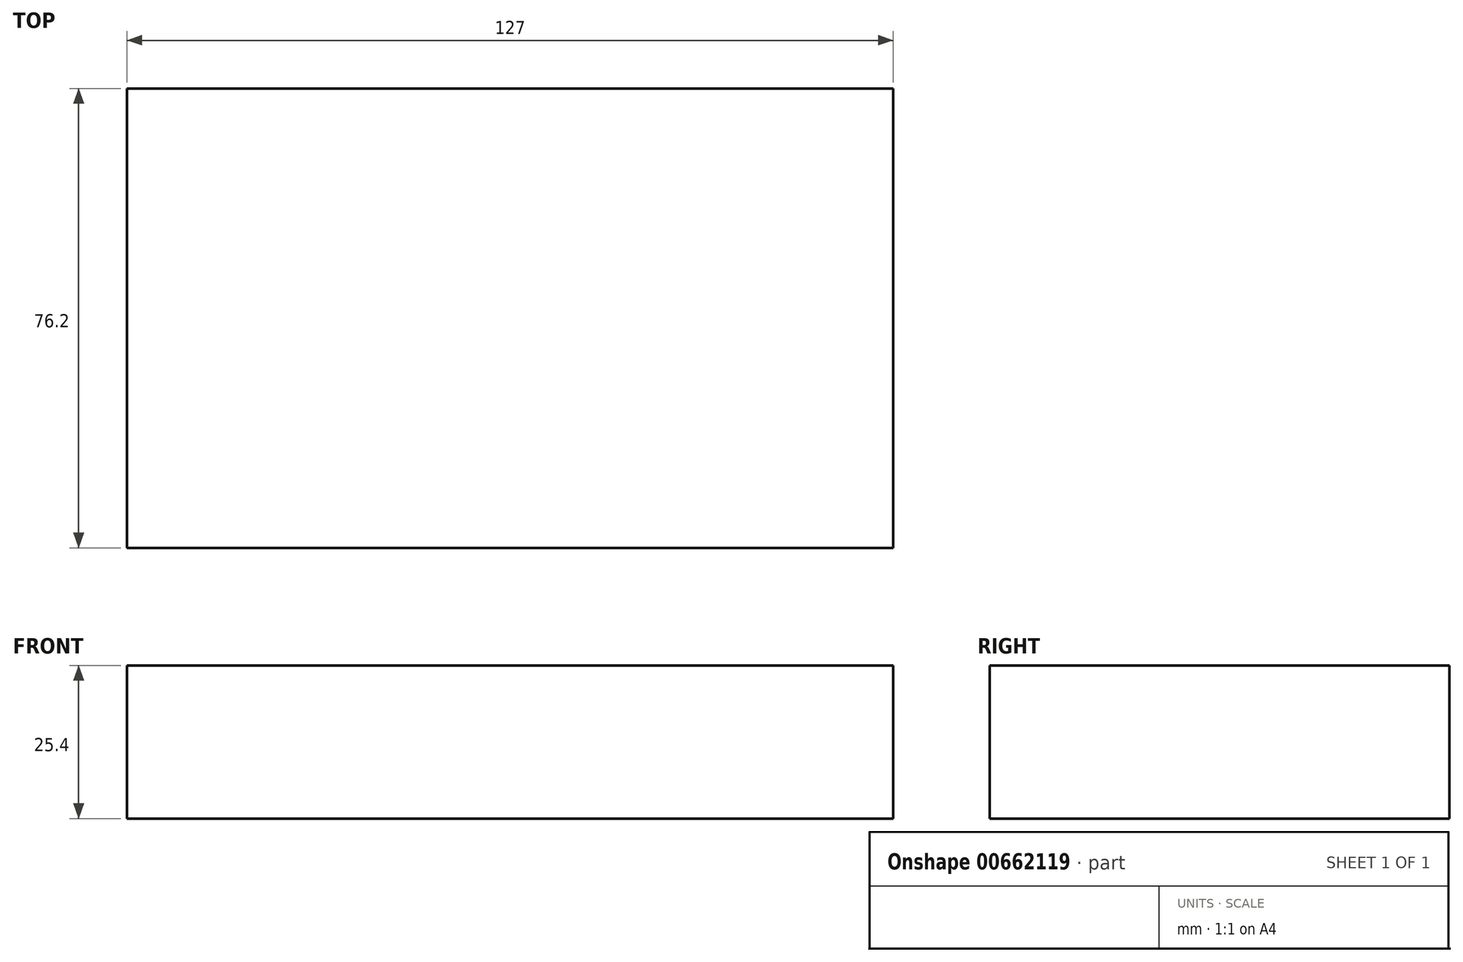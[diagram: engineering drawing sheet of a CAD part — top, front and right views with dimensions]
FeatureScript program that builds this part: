
annotation { "Feature Type Name" : "Feature", "Feature Type Description" : "" }
export const myFeature = defineFeature(function(context is Context, id is Id, definition is map)
    precondition{}
    {
        {
            var Q0;
            Q0=qCreatedBy(makeId("Right.planeOp"),FACE);
            var sketch = newSketch(context, id + "F0", { "sketchPlane" : qUnion([Q0])});
            skLineSegment(sketch, "E0.bottom", {"start": v(-29.83, 10.92) * mm, "end": v(46.37, 10.92) * mm});
            skLineSegment(sketch, "E0.top", {"start": v(-29.83, -14.48) * mm, "end": v(46.37, -14.48) * mm});
            skLineSegment(sketch, "E0.left", {"start": v(-29.83, 10.92) * mm, "end": v(-29.83, -14.48) * mm});
            skLineSegment(sketch, "E0.right", {"start": v(46.37, 10.92) * mm, "end": v(46.37, -14.48) * mm});
            skSolve(sketch);
        }
        {
            var Q0;
            Q0 = qSketchRegion(id + "F0", true);
            extrude(context, id + "F1", {"entities" : qUnion([Q0]), "endBound" : BoundingType.SYMMETRIC, "depth" : 127 * mm, "offsetDistance" : 25.4 * mm});
        }
    });
